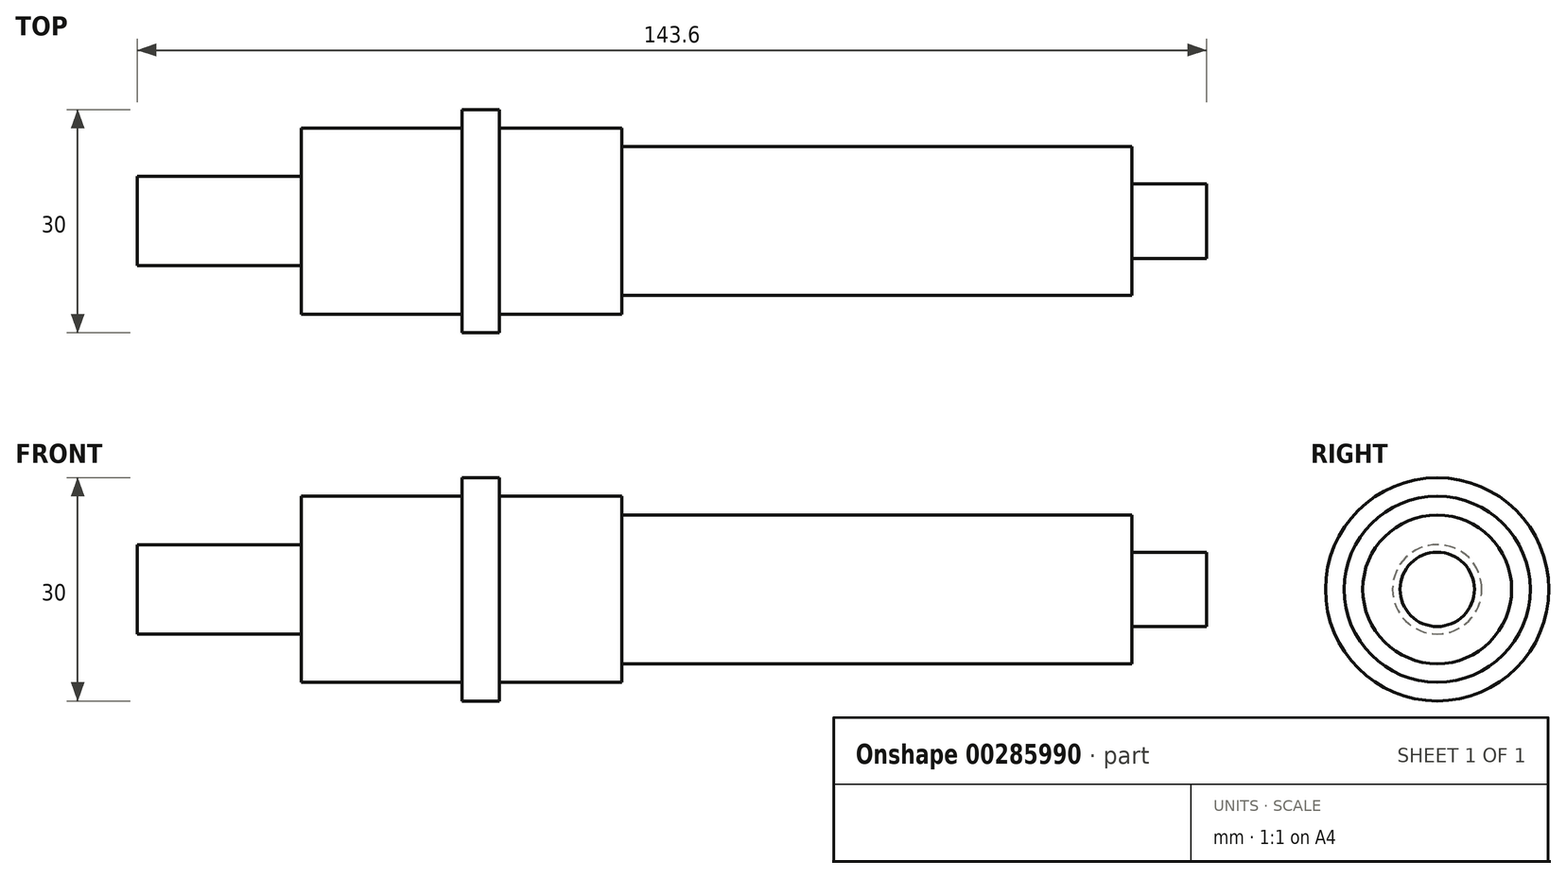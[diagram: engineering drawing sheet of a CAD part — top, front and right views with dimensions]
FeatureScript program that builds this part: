
annotation { "Feature Type Name" : "Feature", "Feature Type Description" : "" }
export const myFeature = defineFeature(function(context is Context, id is Id, definition is map)
    precondition{}
    {
        {
            var Q0;
            Q0=qCreatedBy(makeId("Top.planeOp"),FACE);
            var sketch = newSketch(context, id + "F0", { "sketchPlane" : qUnion([Q0])});
            skLineSegment(sketch, "E0", {"start": v(-66.8, 0) * mm, "end": v(66.8, 0) * mm});
            skLineSegment(sketch, "E1", {"start": v(66.8, 5) * mm, "end": v(66.8, 10) * mm});
            skLineSegment(sketch, "E2", {"start": v(66.8, 10) * mm, "end": v(-1.7, 10) * mm});
            skLineSegment(sketch, "E3", {"start": v(-1.7, 10) * mm, "end": v(-1.7, 12.5) * mm});
            skLineSegment(sketch, "E4", {"start": v(-1.7, 12.5) * mm, "end": v(-18.2, 12.5) * mm});
            skLineSegment(sketch, "E5", {"start": v(-18.2, 12.5) * mm, "end": v(-18.2, 15) * mm});
            skLineSegment(sketch, "E6", {"start": v(-18.2, 15) * mm, "end": v(-23.2, 15) * mm});
            skLineSegment(sketch, "E7", {"start": v(-23.2, 15) * mm, "end": v(-23.2, 12.5) * mm});
            skLineSegment(sketch, "E8", {"start": v(-66.8, 6) * mm, "end": v(-66.8, 0) * mm});
            skLineSegment(sketch, "E9", {"start": v(66.8, 5) * mm, "end": v(76.8, 5) * mm});
            skLineSegment(sketch, "E10", {"start": v(76.8, 5) * mm, "end": v(76.8, 0) * mm});
            skLineSegment(sketch, "E11", {"start": v(76.8, 0) * mm, "end": v(66.8, 0) * mm});
            skLineSegment(sketch, "E12", {"start": v(-66.8, 6) * mm, "end": v(-44.8, 6) * mm});
            skLineSegment(sketch, "E13", {"start": v(-44.8, 6) * mm, "end": v(-44.8, 12.5) * mm});
            skLineSegment(sketch, "E14", {"start": v(-44.8, 12.5) * mm, "end": v(-23.2, 12.5) * mm});
            skSolve(sketch);
        }
        {
            var Q0;
            Q0=makeQuery(id+"F0.imprint","IMPRINT",FACE,{"disambiguationData":[TD([[makeQuery(id+"F0.imprint","IMPRINT",EDGE,{"derivedFrom":sQuery(id+"F0.wireOp",EDGE,"E0")}),1.0]])]});
            var Q1;
            Q1=sQuery(id+"F0.wireOp",EDGE,"E0");
            revolve(context, id + "F1", {"entities" : qUnion([Q0]), "axis" : qUnion([Q1]), "revolveType" : RevolveType.FULL});
        }
    });
